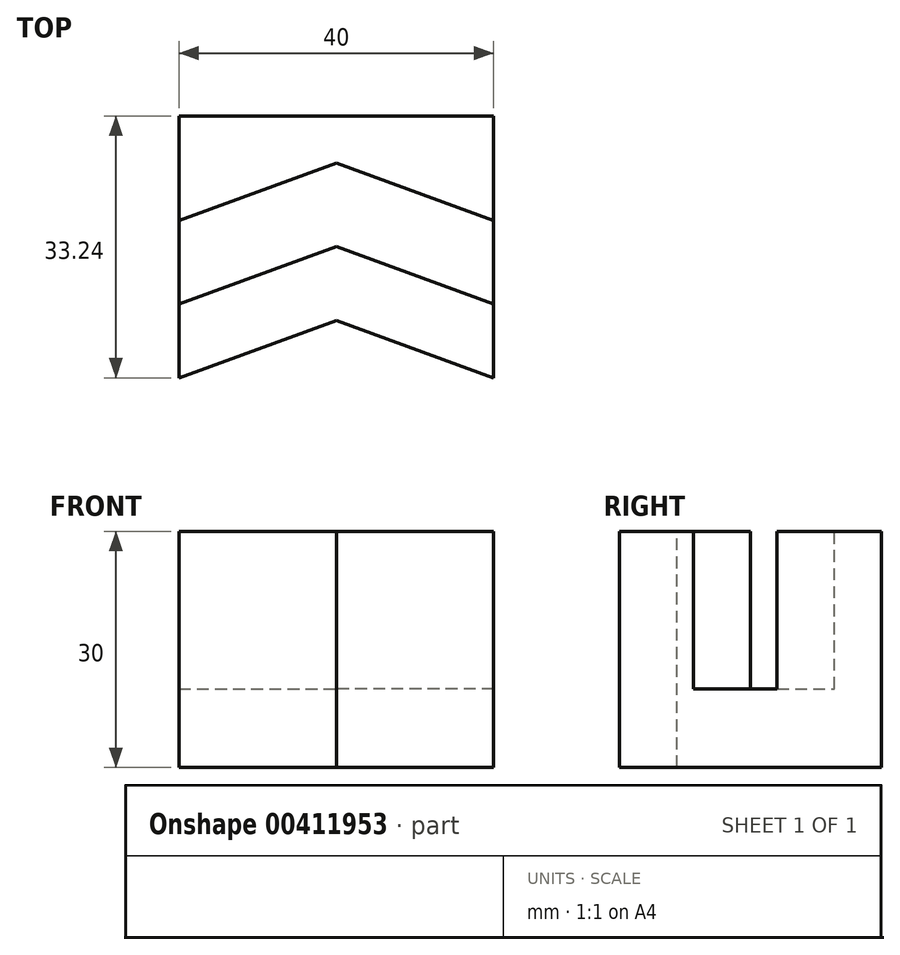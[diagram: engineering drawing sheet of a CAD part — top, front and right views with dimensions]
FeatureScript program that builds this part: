
annotation { "Feature Type Name" : "Feature", "Feature Type Description" : "" }
export const myFeature = defineFeature(function(context is Context, id is Id, definition is map)
    precondition{}
    {
        {
            var Q0;
            Q0=qCreatedBy(makeId("Top.planeOp"),FACE);
            var sketch = newSketch(context, id + "F0", { "sketchPlane" : qUnion([Q0])});
            skLineSegment(sketch, "E0.bottom", {"start": v(20, 20) * mm, "end": v(-20, 20) * mm});
            skLineSegment(sketch, "E0.top", {"start": v(20, -20) * mm, "end": v(-20, -20) * mm});
            skLineSegment(sketch, "E0.left", {"start": v(20, 20) * mm, "end": v(20, -20) * mm});
            skLineSegment(sketch, "E0.right", {"start": v(-20, 20) * mm, "end": v(-20, -20) * mm});
            skPoint(sketch, "E0.middle", {"position": v(0, 0) * mm});
            skSolve(sketch);
        }
        {
            var Q0;
            Q0 = qSketchRegion(id + "F0", true);
            extrude(context, id + "F1", {"entities" : qUnion([Q0]), "oppositeDirection" : true, "depth" : 30 * mm});
        }
        {
            var Q0;
            Q0=makeQuery(id+"F1.opExtrude","CAP_FACE",FACE,{"disambiguationData":[OSD([sQuery(id+"F0.wireOp",EDGE,"E0.bottom"),sQuery(id+"F0.wireOp",EDGE,"E0.top"),sQuery(id+"F0.wireOp",EDGE,"E0.left"),sQuery(id+"F0.wireOp",EDGE,"E0.right")])],"isStart":true});
            var sketch = newSketch(context, id + "F2", { "sketchPlane" : qUnion([Q0])});
            skLineSegment(sketch, "E1", {"start": v(20, 0) * mm, "end": v(0, 7.28) * mm});
            skLineSegment(sketch, "E2", {"start": v(20, -10.64) * mm, "end": v(0, -3.36) * mm});
            skLineSegment(sketch, "E3.MirrorCS", {"start": v(-20, 0) * mm, "end": v(0, 7.28) * mm});
            skLineSegment(sketch, "E4.MirrorCS", {"start": v(-20, -10.64) * mm, "end": v(0, -3.36) * mm});
            skLineSegment(sketch, "E5", {"start": v(20, -20) * mm, "end": v(0, -12.72) * mm});
            skLineSegment(sketch, "E6", {"start": v(0, -12.72) * mm, "end": v(-20, -20) * mm});
            skLineSegment(sketch, "E7", {"start": v(20, 13.24) * mm, "end": v(-20, 13.24) * mm});
            skSolve(sketch);
        }
        {
            var Q0;
            {var subQ4=sQuery(id+"F2.wireOp",EDGE,"E1");Q0=makeQuery(id+"F2.imprint","IMPRINT",FACE,{"disambiguationData":[TD([[makeQuery(id+"F2.imprint","IMPRINT",EDGE,{"derivedFrom":subQ4}),1.0]])]});}
            extrude(context, id + "F3", {"entities" : qUnion([Q0]), "operationType" : NewBodyOperationType.REMOVE, "oppositeDirection" : true, "depth" : 20 * mm});
        }
        {
            var Q0;
            Q0=makeQuery(id+"F2.imprint","IMPRINT",FACE,{"disambiguationData":[TD([[makeQuery(id+"F2.imprint","IMPRINT",EDGE,{"derivedFrom":sQuery(id+"F2.wireOp",EDGE,"E5")}),1.0]])]});
            var Q1;
            {var subQ0=sQuery(id+"F2.wireOp",EDGE,"E7");Q1=makeQuery(id+"F2.imprint","IMPRINT",FACE,{"disambiguationData":[TD([[makeQuery(id+"F2.imprint","IMPRINT",EDGE,{"derivedFrom":subQ0}),-1.0]])]});}
            extrude(context, id + "F4", {"entities" : qUnion([Q0, Q1]), "operationType" : NewBodyOperationType.REMOVE, "endBound" : BoundingType.THROUGH_ALL, "oppositeDirection" : true, "depth" : 25 * mm});
        }
    });
